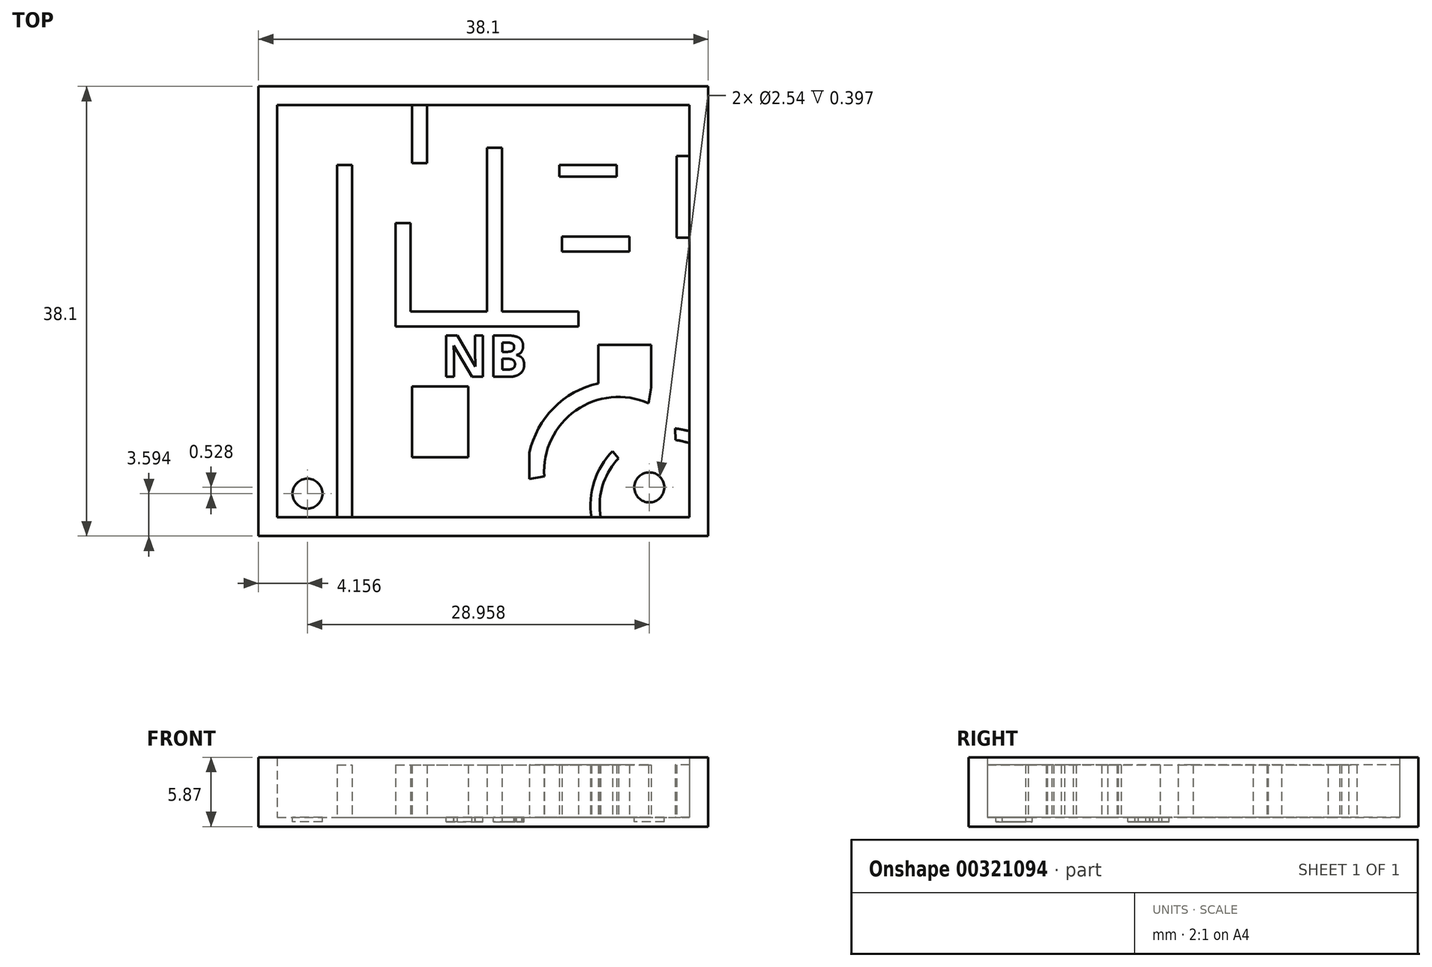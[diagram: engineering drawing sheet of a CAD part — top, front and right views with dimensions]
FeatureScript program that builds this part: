
annotation { "Feature Type Name" : "Feature", "Feature Type Description" : "" }
export const myFeature = defineFeature(function(context is Context, id is Id, definition is map)
    precondition{}
    {
        {
            var Q0;
            Q0=qCreatedBy(makeId("Top.planeOp"),FACE);
            var sketch = newSketch(context, id + "F0", { "sketchPlane" : qUnion([Q0])});
            skLineSegment(sketch, "E0.bottom", {"start": v(-17.92, 8.98) * mm, "end": v(20.18, 8.98) * mm});
            skLineSegment(sketch, "E0.top", {"start": v(-17.92, -29.12) * mm, "end": v(20.18, -29.12) * mm});
            skLineSegment(sketch, "E0.left", {"start": v(-17.92, 8.98) * mm, "end": v(-17.92, -29.12) * mm});
            skLineSegment(sketch, "E0.right", {"start": v(20.18, 8.98) * mm, "end": v(20.18, -29.12) * mm});
            skSolve(sketch);
        }
        {
            var Q0;
            Q0=makeQuery(id+"F0.imprint","IMPRINT",FACE,{"disambiguationData":[TD([[makeQuery(id+"F0.imprint","IMPRINT",EDGE,{"derivedFrom":sQuery(id+"F0.wireOp",EDGE,"E0.bottom")}),-1.0]])]});
            extrude(context, id + "F1", {"entities" : qUnion([Q0]), "depth" : 0.8 * mm});
        }
        {
            var Q0;
            Q0=makeQuery(id+"F1.opExtrude","CAP_FACE",FACE,{"disambiguationData":[OSD([sQuery(id+"F0.wireOp",EDGE,"E0.bottom"),sQuery(id+"F0.wireOp",EDGE,"E0.top"),sQuery(id+"F0.wireOp",EDGE,"E0.left"),sQuery(id+"F0.wireOp",EDGE,"E0.right")])],"isStart":false});
            var sketch = newSketch(context, id + "F2", { "sketchPlane" : qUnion([Q0])});
            skLineSegment(sketch, "E1.0", {"start": v(-16.33, 7.4) * mm, "end": v(18.6, 7.4) * mm});
            skLineSegment(sketch, "E1.1", {"start": v(-16.33, 7.4) * mm, "end": v(-16.33, -27.53) * mm});
            skLineSegment(sketch, "E1.2", {"start": v(-16.33, -27.53) * mm, "end": v(18.6, -27.53) * mm});
            skLineSegment(sketch, "E1.3", {"start": v(18.6, 7.4) * mm, "end": v(18.6, -27.53) * mm});
            skSolve(sketch);
        }
        {
            var Q0;
            Q0=makeQuery(id+"F2.imprint","IMPRINT",FACE,{"disambiguationData":[TD([[makeQuery(id+"F2.imprint","IMPRINT",EDGE,{"derivedFrom":sQuery(id+"F2.wireOp",EDGE,"E1.0")}),1.0]])]});
            extrude(context, id + "F3", {"entities" : qUnion([Q0]), "operationType" : NewBodyOperationType.ADD, "depth" : 5.08 * mm});
        }
        {
            var Q0;
            Q0=makeQuery(id+"F1.opExtrude","CAP_FACE",FACE,{"disambiguationData":[OSD([sQuery(id+"F0.wireOp",EDGE,"E0.bottom"),sQuery(id+"F0.wireOp",EDGE,"E0.top"),sQuery(id+"F0.wireOp",EDGE,"E0.left"),sQuery(id+"F0.wireOp",EDGE,"E0.right")])],"isStart":false});
            var sketch = newSketch(context, id + "F4", { "sketchPlane" : qUnion([Q0])});
            skLineSegment(sketch, "E2.bottom", {"start": v(-11.25, -27.53) * mm, "end": v(-9.98, -27.53) * mm});
            skLineSegment(sketch, "E2.top", {"start": v(-11.25, 2.32) * mm, "end": v(-9.98, 2.32) * mm});
            skLineSegment(sketch, "E2.left", {"start": v(-11.25, -27.53) * mm, "end": v(-11.25, 2.32) * mm});
            skLineSegment(sketch, "E2.right", {"start": v(-9.98, -27.53) * mm, "end": v(-9.98, 2.32) * mm});
            skLineSegment(sketch, "E3.bottom", {"start": v(-4.9, 7.4) * mm, "end": v(-3.63, 7.4) * mm});
            skLineSegment(sketch, "E4.bottom", {"start": v(-5.02, -10.1) * mm, "end": v(1.45, -10.1) * mm});
            skLineSegment(sketch, "E4.top", {"start": v(-2.24, -11.37) * mm, "end": v(9.2, -11.37) * mm});
            skLineSegment(sketch, "E4.left", {"start": v(-6.29, -10.1) * mm, "end": v(-6.29, -11.37) * mm});
            skLineSegment(sketch, "E4.right", {"start": v(9.2, -10.1) * mm, "end": v(9.2, -11.37) * mm});
            skLineSegment(sketch, "E5.top", {"start": v(1.45, 3.78) * mm, "end": v(2.72, 3.78) * mm});
            skLineSegment(sketch, "E5.left", {"start": v(1.45, -10.1) * mm, "end": v(1.45, 3.78) * mm});
            skLineSegment(sketch, "E5.right", {"start": v(2.72, -10.1) * mm, "end": v(2.72, 3.78) * mm});
            skLineSegment(sketch, "E6.bottom", {"start": v(13.52, -3.75) * mm, "end": v(7.8, -3.75) * mm});
            skLineSegment(sketch, "E6.top", {"start": v(13.52, -5.02) * mm, "end": v(7.8, -5.02) * mm});
            skLineSegment(sketch, "E6.left", {"start": v(13.52, -3.75) * mm, "end": v(13.52, -5.02) * mm});
            skLineSegment(sketch, "E6.right", {"start": v(7.8, -3.75) * mm, "end": v(7.8, -5.02) * mm});
            skPoint(sketch, "E3.top.start.orphan", {"position": v(-4.9, -13.82) * mm});
            skLineSegment(sketch, "E7.trimOffspring", {"start": v(2.72, -10.1) * mm, "end": v(9.2, -10.1) * mm});
            skPoint(sketch, "E5.bottom.start.orphan", {"position": v(1.45, -11.37) * mm});
            skLineSegment(sketch, "E8", {"start": v(-6.29, -11.37) * mm, "end": v(-2.24, -11.37) * mm});
            skLineSegment(sketch, "E9", {"start": v(-4.9, 7.4) * mm, "end": v(-4.9, 2.48) * mm});
            skLineSegment(sketch, "E10", {"start": v(-4.9, 2.48) * mm, "end": v(-3.63, 2.48) * mm});
            skLineSegment(sketch, "E11", {"start": v(-3.63, 2.48) * mm, "end": v(-3.63, 7.4) * mm});
            skLineSegment(sketch, "E12", {"start": v(-6.29, -10.1) * mm, "end": v(-6.29, -2.6) * mm});
            skLineSegment(sketch, "E13", {"start": v(-6.29, -2.6) * mm, "end": v(-5.02, -2.6) * mm});
            skLineSegment(sketch, "E14", {"start": v(-5.02, -2.6) * mm, "end": v(-5.02, -10.1) * mm});
            skLineSegment(sketch, "E15.bottom", {"start": v(7.59, 2.32) * mm, "end": v(12.43, 2.32) * mm});
            skLineSegment(sketch, "E15.top", {"start": v(7.59, 1.33) * mm, "end": v(12.43, 1.33) * mm});
            skLineSegment(sketch, "E15.left", {"start": v(7.59, 2.32) * mm, "end": v(7.59, 1.33) * mm});
            skLineSegment(sketch, "E15.right", {"start": v(12.43, 2.32) * mm, "end": v(12.43, 1.33) * mm});
            skLineSegment(sketch, "E16.bottom", {"start": v(-4.9, -16.45) * mm, "end": v(-0.15, -16.45) * mm});
            skLineSegment(sketch, "E16.top", {"start": v(-4.9, -22.45) * mm, "end": v(-0.15, -22.45) * mm});
            skLineSegment(sketch, "E16.left", {"start": v(-4.9, -16.45) * mm, "end": v(-4.9, -22.45) * mm});
            skLineSegment(sketch, "E16.right", {"start": v(-0.15, -16.45) * mm, "end": v(-0.15, -22.45) * mm});
            skArc(sketch, "E17", {"start": v(15.36, -16.55) * mm, "mid": v(8.91, -16.91) * mm, "end": v(5.04, -22.08) * mm});
            skArc(sketch, "E18", {"start": v(18.6, -20.25) * mm, "mid": v(17.99, -20.1) * mm, "end": v(17.37, -20) * mm});
            skLineSegment(sketch, "E19.bottom", {"start": v(10.86, -12.91) * mm, "end": v(15.36, -12.91) * mm});
            skLineSegment(sketch, "E19.left", {"start": v(10.86, -12.91) * mm, "end": v(10.86, -16.19) * mm});
            skLineSegment(sketch, "E19.right", {"start": v(15.36, -12.91) * mm, "end": v(15.36, -16.55) * mm});
            skLineSegment(sketch, "E20", {"start": v(15.36, -15.18) * mm, "end": v(15.36, -16.55) * mm});
            skLineSegment(sketch, "E21", {"start": v(18.6, -19.56) * mm, "end": v(18.6, -15.18) * mm});
            skArc(sketch, "E22.trimOffspring", {"start": v(15.36, -16.55) * mm, "mid": v(13.14, -16.03) * mm, "end": v(10.86, -16.19) * mm});
            skLineSegment(sketch, "E23.top", {"start": v(3.69, -27.53) * mm, "end": v(5.4, -27.53) * mm});
            skLineSegment(sketch, "E24.right", {"start": v(18.6, -16.35) * mm, "end": v(18.6, -19) * mm});
            skPoint(sketch, "E25.start.orphan", {"position": v(19.3, -19.76) * mm});
            skLineSegment(sketch, "E26", {"start": v(5.04, -22.08) * mm, "end": v(5.04, -24.3) * mm});
            skArc(sketch, "E27.trimOffspring", {"start": v(12.09, -21.92) * mm, "mid": v(10.52, -24.51) * mm, "end": v(10.29, -27.53) * mm});
            skArc(sketch, "E28", {"start": v(15.12, -17.86) * mm, "mid": v(8.96, -18.48) * mm, "end": v(6.29, -24.06) * mm});
            skLineSegment(sketch, "E29", {"start": v(5.04, -24.3) * mm, "end": v(6.29, -24.06) * mm});
            skLineSegment(sketch, "E30", {"start": v(15.12, -17.86) * mm, "end": v(15.36, -16.55) * mm});
            skArc(sketch, "E31.0", {"start": v(18.82, -21.35) * mm, "mid": v(18.13, -21.12) * mm, "end": v(17.42, -20.99) * mm});
            skLineSegment(sketch, "E32", {"start": v(18.6, -21.26) * mm, "end": v(18.82, -21.35) * mm});
            skArc(sketch, "E33.0", {"start": v(12.58, -22.54) * mm, "mid": v(11.33, -24.57) * mm, "end": v(11.01, -26.94) * mm});
            skLineSegment(sketch, "E34", {"start": v(12.09, -21.92) * mm, "end": v(12.58, -22.54) * mm});
            skLineSegment(sketch, "E35", {"start": v(17.37, -20) * mm, "end": v(17.42, -20.99) * mm});
            skLineSegment(sketch, "E36", {"start": v(11.01, -26.94) * mm, "end": v(11.05, -27.53) * mm});
            skSolve(sketch);
        }
        {
            var Q0;
            Q0=makeQuery(id+"F4.imprint","IMPRINT",FACE,{"disambiguationData":[TD([[makeQuery(id+"F4.imprint","IMPRINT",EDGE,{"derivedFrom":sQuery(id+"F4.wireOp",EDGE,"E2.top")}),1.0]])]});
            var sketch = newSketch(context, id + "F5", { "sketchPlane" : qUnion([Q0])});
            skText(sketch, "E37", { "text": "NB", "fontName": "OpenSans-Bold.ttf"});
            const initialGuessF5  = {"E37": [-0.00245, -0.01563, 1, 0, 0.00354]};
            skSetInitialGuess(sketch, initialGuessF5);
            skSolve(sketch);
        }
        {
            var Q0;
            Q0 = qSketchRegion(id + "F5", true);
            extrude(context, id + "F6", {"entities" : qUnion([Q0]), "operationType" : NewBodyOperationType.REMOVE, "oppositeDirection" : true, "depth" : 0.4 * mm});
        }
        {
            var Q0;
            Q0=makeQuery(id+"F4.imprint","IMPRINT",FACE,{"disambiguationData":[TD([[makeQuery(id+"F4.imprint","IMPRINT",EDGE,{"derivedFrom":sQuery(id+"F4.wireOp",EDGE,"E2.top")}),1.0]])]});
            var sketch = newSketch(context, id + "F7", { "sketchPlane" : qUnion([Q0])});
            skLineSegment(sketch, "E38", {"start": v(-16.3, -27.57) * mm, "end": v(-11.23, -27.57) * mm});
            skCircle(sketch, "E39", {"center": v(-13.76, -25.53) * mm, "radius": 1.27 * mm});
            skPoint(sketch, "E39.centerSnap0", {"position": v(-13.76, -27.57) * mm});
            skCircle(sketch, "E40", {"center": v(13.06, -25.68) * mm, "radius": 1.27 * mm});
            skSolve(sketch);
        }
        {
            var Q0;
            Q0=makeQuery(id+"F7.imprint","IMPRINT",FACE,{"disambiguationData":[TD([[makeQuery(id+"F7.imprint","IMPRINT",EDGE,{"derivedFrom":sQuery(id+"F7.wireOp",EDGE,"E39")}),1.0]])]});
            extrude(context, id + "F8", {"entities" : qUnion([Q0]), "operationType" : NewBodyOperationType.REMOVE, "oppositeDirection" : true, "depth" : 0.4 * mm});
        }
        {
            var Q0;
            Q0=makeQuery(id+"F4.imprint","IMPRINT",FACE,{"disambiguationData":[TD([[makeQuery(id+"F4.imprint","IMPRINT",EDGE,{"derivedFrom":sQuery(id+"F4.wireOp",EDGE,"E2.top")}),1.0]])]});
            var sketch = newSketch(context, id + "F9", { "sketchPlane" : qUnion([Q0])});
            skCircle(sketch, "E41", {"center": v(15.2, -25) * mm, "radius": 1.27 * mm});
            skSolve(sketch);
        }
        {
            var Q0;
            Q0 = qSketchRegion(id + "F9", true);
            extrude(context, id + "F10", {"entities" : qUnion([Q0]), "operationType" : NewBodyOperationType.REMOVE, "oppositeDirection" : true, "depth" : 0.4 * mm});
        }
        {
            var Q0;
            Q0=makeQuery(id+"F4.imprint","IMPRINT",FACE,{"disambiguationData":[TD([[makeQuery(id+"F4.imprint","IMPRINT",EDGE,{"derivedFrom":sQuery(id+"F4.wireOp",EDGE,"E2.bottom")}),1.0]])]});
            var Q1;
            Q1=makeQuery(id+"F4.imprint","IMPRINT",FACE,{"disambiguationData":[TD([[makeQuery(id+"F4.imprint","IMPRINT",EDGE,{"derivedFrom":sQuery(id+"F4.wireOp",EDGE,"E4.bottom")}),-1.0]])]});
            var Q2;
            Q2=makeQuery(id+"F4.imprint","IMPRINT",FACE,{"disambiguationData":[TD([[makeQuery(id+"F4.imprint","IMPRINT",EDGE,{"derivedFrom":sQuery(id+"F4.wireOp",EDGE,"E3.bottom")}),-1.0]])]});
            var Q3;
            Q3=makeQuery(id+"F4.imprint","IMPRINT",FACE,{"disambiguationData":[TD([[makeQuery(id+"F4.imprint","IMPRINT",EDGE,{"derivedFrom":sQuery(id+"F4.wireOp",EDGE,"E15.bottom")}),-1.0]])]});
            var Q4;
            Q4=makeQuery(id+"F4.imprint","IMPRINT",FACE,{"disambiguationData":[TD([[makeQuery(id+"F4.imprint","IMPRINT",EDGE,{"derivedFrom":sQuery(id+"F4.wireOp",EDGE,"E6.bottom")}),1.0]])]});
            var Q5;
            Q5=makeQuery(id+"F4.imprint","IMPRINT",FACE,{"disambiguationData":[TD([[makeQuery(id+"F4.imprint","IMPRINT",EDGE,{"derivedFrom":sQuery(id+"F4.wireOp",EDGE,"E19.bottom")}),-1.0]])]});
            var Q6;
            Q6=makeQuery(id+"F4.imprint","IMPRINT",FACE,{"disambiguationData":[TD([[makeQuery(id+"F4.imprint","IMPRINT",EDGE,{"derivedFrom":sQuery(id+"F4.wireOp",EDGE,"E17")}),1.0]])]});
            var Q7;
            Q7=makeQuery(id+"F4.imprint","IMPRINT",FACE,{"disambiguationData":[TD([[makeQuery(id+"F4.imprint","IMPRINT",EDGE,{"derivedFrom":sQuery(id+"F4.wireOp",EDGE,"E16.bottom")}),-1.0]])]});
            var Q8;
            {var subQ0=sQuery(id+"F4.wireOp",EDGE,"E27.trimOffspring");Q8=makeQuery(id+"F4.imprint","IMPRINT",FACE,{"disambiguationData":[TD([[makeQuery(id+"F4.imprint","IMPRINT",EDGE,{"derivedFrom":subQ0}),1.0]])]});}
            var Q9;
            {var subQ0=sQuery(id+"F4.wireOp",EDGE,"E18");Q9=makeQuery(id+"F4.imprint","IMPRINT",FACE,{"disambiguationData":[TD([[makeQuery(id+"F4.imprint","IMPRINT",EDGE,{"derivedFrom":subQ0}),1.0]])]});}
            extrude(context, id + "F11", {"entities" : qUnion([Q0, Q1, Q2, Q3, Q4, Q5, Q6, Q7, Q8, Q9]), "operationType" : NewBodyOperationType.ADD, "depth" : 4.44 * mm});
        }
        {
            var Q0;
            Q0=makeQuery(id+"F6.boolean.opBoolean","SPLIT",FACE,{"disambiguationData":[TD([makeQuery(id+"F3.opExtrude","SWEPT_FACE",FACE,{"disambiguationData":[OSD([sQuery(id+"F2.wireOp",EDGE,"E1.0")])]})])],"derivedFrom":makeQuery(id+"F1.opExtrude","CAP_FACE",FACE,{"disambiguationData":[OSD([sQuery(id+"F0.wireOp",EDGE,"E0.bottom"),sQuery(id+"F0.wireOp",EDGE,"E0.top"),sQuery(id+"F0.wireOp",EDGE,"E0.left"),sQuery(id+"F0.wireOp",EDGE,"E0.right")])],"isStart":false})});
            var sketch = newSketch(context, id + "F12", { "sketchPlane" : qUnion([Q0])});
            skLineSegment(sketch, "E42.bottom", {"start": v(18.6, 3.08) * mm, "end": v(17.5, 3.08) * mm});
            skLineSegment(sketch, "E42.top", {"start": v(18.6, -3.84) * mm, "end": v(17.5, -3.84) * mm});
            skLineSegment(sketch, "E42.left", {"start": v(18.6, 3.08) * mm, "end": v(18.6, -3.84) * mm});
            skLineSegment(sketch, "E42.right", {"start": v(17.5, 3.08) * mm, "end": v(17.5, -3.84) * mm});
            skSolve(sketch);
        }
        {
            var Q0;
            Q0=makeQuery(id+"F12.imprint","IMPRINT",FACE,{"disambiguationData":[TD([[makeQuery(id+"F12.imprint","IMPRINT",EDGE,{"derivedFrom":sQuery(id+"F12.wireOp",EDGE,"E42.bottom")}),1.0]])]});
            extrude(context, id + "F13", {"entities" : qUnion([Q0]), "operationType" : NewBodyOperationType.ADD, "depth" : 4.44 * mm});
        }
    });
